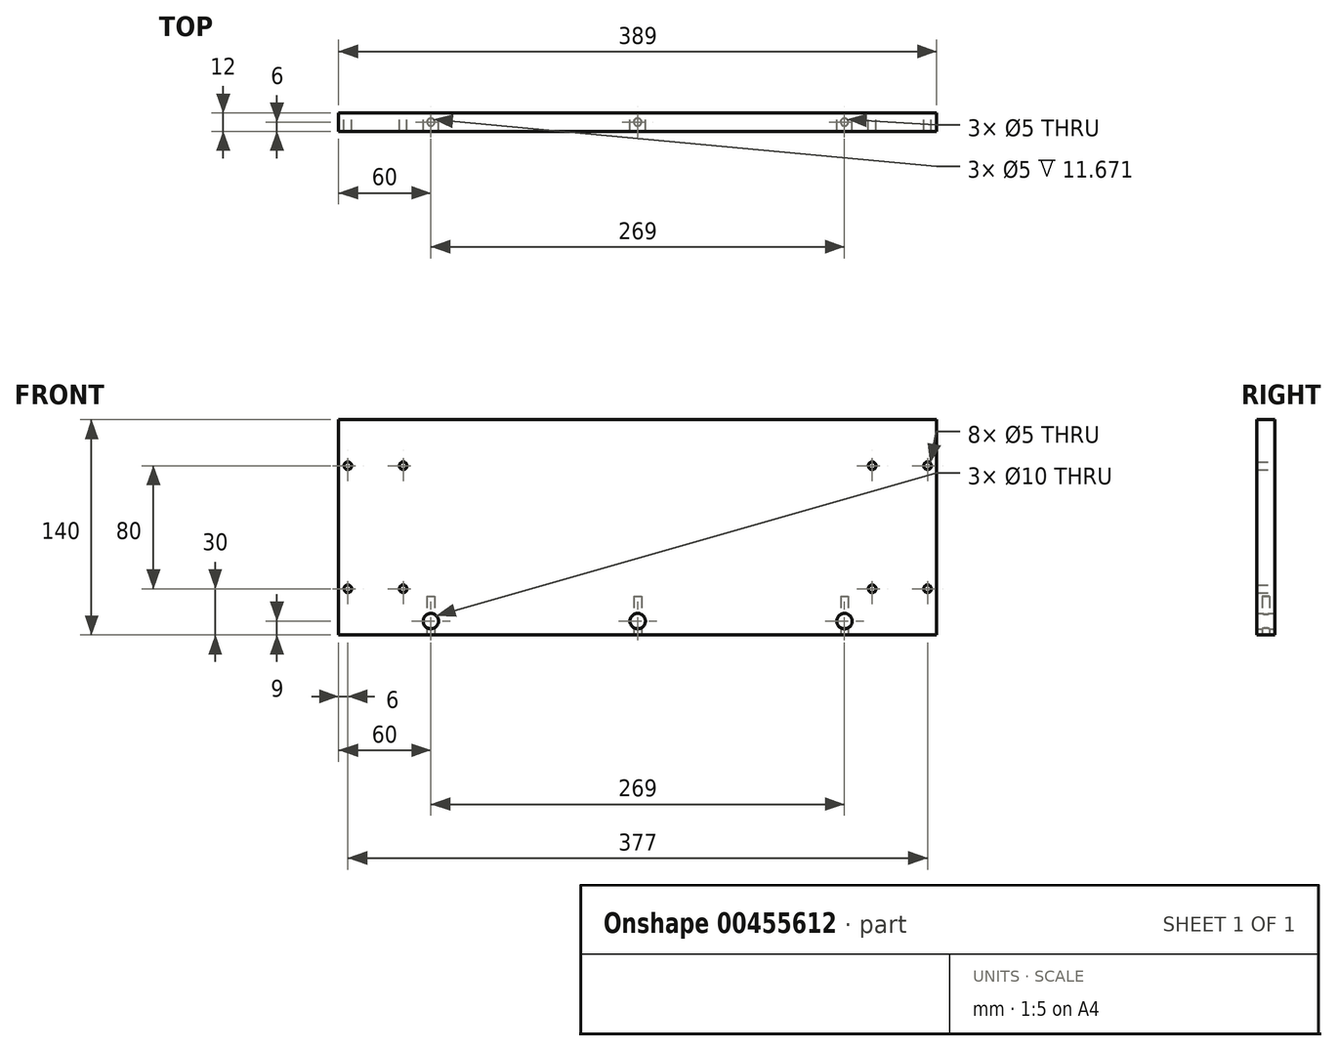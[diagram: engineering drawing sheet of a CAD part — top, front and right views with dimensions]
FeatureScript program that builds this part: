
annotation { "Feature Type Name" : "Feature", "Feature Type Description" : "" }
export const myFeature = defineFeature(function(context is Context, id is Id, definition is map)
    precondition{}
    {
        {
            var Q0;
            Q0=qCreatedBy(makeId("Front.planeOp"),FACE);
            var sketch = newSketch(context, id + "F0", { "sketchPlane" : qUnion([Q0])});
            skLineSegment(sketch, "E0.bottom", {"start": v(194.5, 70) * mm, "end": v(-194.5, 70) * mm});
            skLineSegment(sketch, "E0.top", {"start": v(194.5, -70) * mm, "end": v(-194.5, -70) * mm});
            skLineSegment(sketch, "E0.left", {"start": v(194.5, 70) * mm, "end": v(194.5, -70) * mm});
            skLineSegment(sketch, "E0.right", {"start": v(-194.5, 70) * mm, "end": v(-194.5, -70) * mm});
            skPoint(sketch, "E0.middle", {"position": v(0, 0) * mm});
            skLineSegment(sketch, "E1", {"start": v(194.5, -61) * mm, "end": v(-194.5, -61) * mm, "construction": true});
            skCircle(sketch, "E2", {"center": v(0, -61) * mm, "radius": 5 * mm});
            skCircle(sketch, "E3", {"center": v(-134.5, -61) * mm, "radius": 5 * mm});
            skCircle(sketch, "E4", {"center": v(134.5, -61) * mm, "radius": 5 * mm});
            skLineSegment(sketch, "E5", {"start": v(-188.5, 70) * mm, "end": v(-188.5, -70) * mm, "construction": true});
            skLineSegment(sketch, "E6", {"start": v(188.5, 70) * mm, "end": v(188.5, -70) * mm, "construction": true});
            skCircle(sketch, "E7", {"center": v(-188.5, 40) * mm, "radius": 2.5 * mm});
            skCircle(sketch, "E8", {"center": v(-188.5, -40) * mm, "radius": 2.5 * mm});
            skCircle(sketch, "E9", {"center": v(188.5, -40) * mm, "radius": 2.5 * mm});
            skCircle(sketch, "E10", {"center": v(188.5, 40) * mm, "radius": 2.5 * mm});
            skCircle(sketch, "E11", {"center": v(-152.5, 40) * mm, "radius": 2.5 * mm});
            skCircle(sketch, "E12", {"center": v(152.5, 40) * mm, "radius": 2.5 * mm});
            skCircle(sketch, "E13", {"center": v(152.5, -40) * mm, "radius": 2.5 * mm});
            skCircle(sketch, "E14", {"center": v(-152.5, -40) * mm, "radius": 2.5 * mm});
            skSolve(sketch);
        }
        {
            var Q0;
            Q0 = qSketchRegion(id + "F0", true);
            extrude(context, id + "F1", {"entities" : qUnion([Q0]), "depth" : 12 * mm});
        }
        {
            var Q0;
            Q0=makeQuery(id+"F1.opExtrude","SWEPT_FACE",FACE,{"disambiguationData":[OSD([sQuery(id+"F0.wireOp",EDGE,"E0.top")])]});
            var sketch = newSketch(context, id + "F2", { "sketchPlane" : qUnion([Q0])});
            skLineSegment(sketch, "E15", {"start": v(-194.5, 6) * mm, "end": v(194.5, 6) * mm, "construction": true});
            skCircle(sketch, "E16", {"center": v(0, 6) * mm, "radius": 2.5 * mm});
            skCircle(sketch, "E17", {"center": v(134.5, 6) * mm, "radius": 2.5 * mm});
            skCircle(sketch, "E18", {"center": v(-134.5, 6) * mm, "radius": 2.5 * mm});
            skSolve(sketch);
        }
        {
            var Q0;
            Q0 = qSketchRegion(id + "F2", true);
            extrude(context, id + "F3", {"entities" : qUnion([Q0]), "operationType" : NewBodyOperationType.REMOVE, "oppositeDirection" : true, "depth" : 25 * mm});
        }
    });
